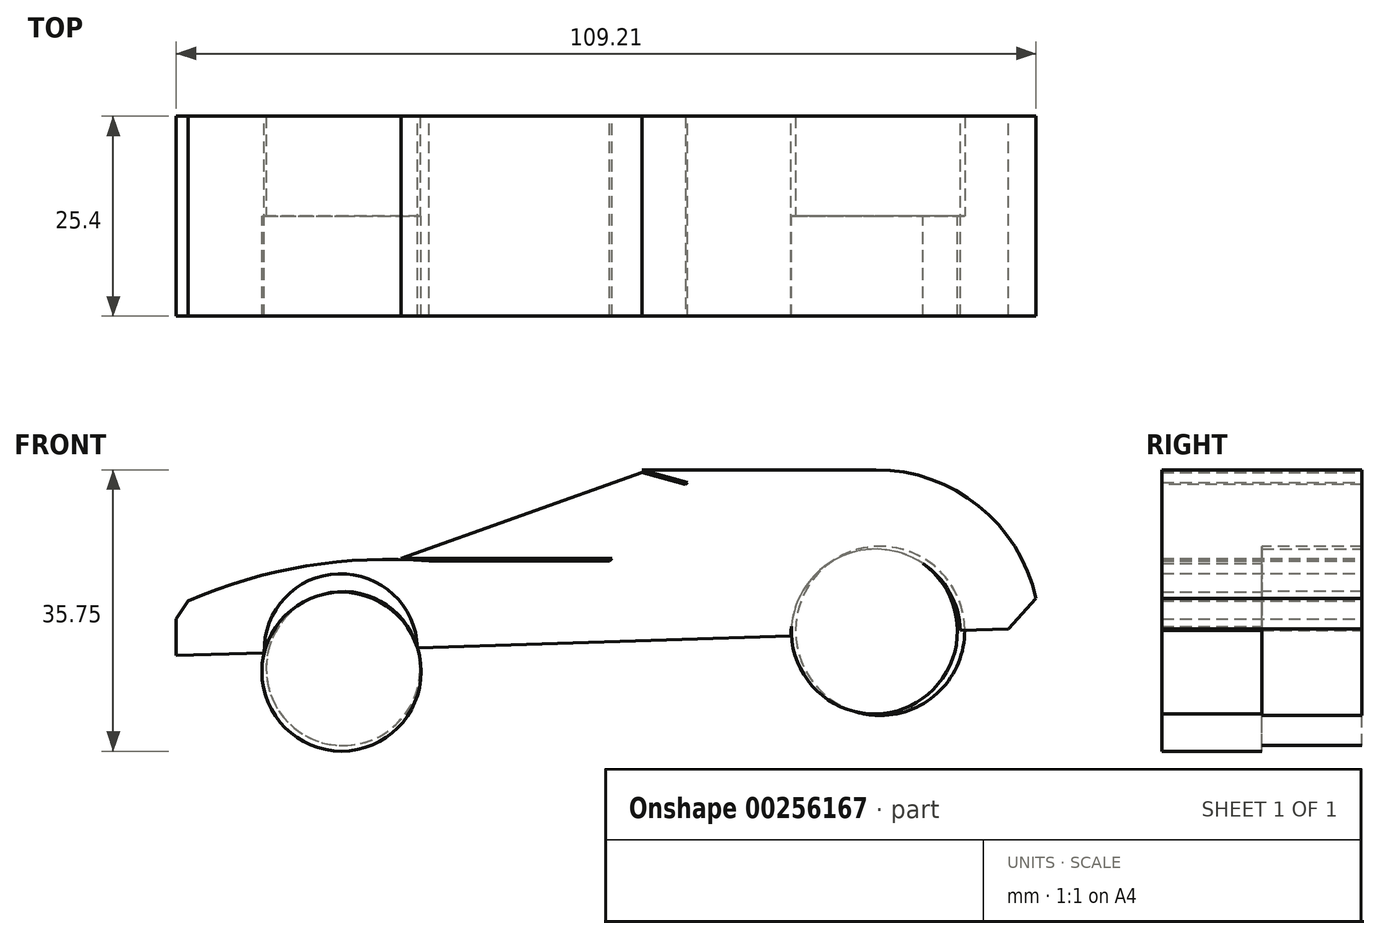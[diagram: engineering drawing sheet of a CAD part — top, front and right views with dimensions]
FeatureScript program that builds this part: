
annotation { "Feature Type Name" : "Feature", "Feature Type Description" : "" }
export const myFeature = defineFeature(function(context is Context, id is Id, definition is map)
    precondition{}
    {
        {
            var Q0;
            Q0=qCreatedBy(makeId("Front.planeOp"),FACE);
            var sketch = newSketch(context, id + "F0", { "sketchPlane" : qUnion([Q0])});
            skLineSegment(sketch, "E0.bottom", {"start": v(-59.18, 0) * mm, "end": v(59.18, 0) * mm});
            skLineSegment(sketch, "E0.top", {"start": v(-59.18, 31.34) * mm, "end": v(59.18, 31.34) * mm});
            skLineSegment(sketch, "E0.left", {"start": v(-59.18, 0) * mm, "end": v(-59.18, 31.34) * mm});
            skLineSegment(sketch, "E0.right", {"start": v(59.18, 0) * mm, "end": v(59.18, 31.34) * mm});
            skPoint(sketch, "E0.middle", {"position": v(0, 15.67) * mm});
            skArc(sketch, "E1", {"start": v(-27.1, 15.49) * mm, "mid": v(-43.51, 14.72) * mm, "end": v(-59.18, 9.77) * mm});
            skLineSegment(sketch, "E2", {"start": v(-27.1, 15.49) * mm, "end": v(0, 27.1) * mm});
            skLineSegment(sketch, "E3", {"start": v(0, 27.1) * mm, "end": v(29.68, 27.1) * mm});
            skArc(sketch, "E4", {"start": v(50.51, 7) * mm, "mid": v(44.15, 21.26) * mm, "end": v(29.68, 27.1) * mm});
            skLineSegment(sketch, "E5", {"start": v(-59.18, 3.5) * mm, "end": v(50.51, 7) * mm});
            skCircle(sketch, "E6", {"center": v(-38.28, 4.17) * mm, "radius": 9.73 * mm});
            skCircle(sketch, "E7", {"center": v(29.68, 6.25) * mm, "radius": 10.76 * mm});
            skLineSegment(sketch, "E8", {"start": v(46.52, 6.88) * mm, "end": v(50.03, 10.76) * mm});
            skLineSegment(sketch, "E9", {"start": v(-27.1, 15.49) * mm, "end": v(-4.17, 15.49) * mm});
            skLineSegment(sketch, "E10", {"start": v(-4.17, 15.49) * mm, "end": v(5.76, 25.5) * mm});
            skLineSegment(sketch, "E11", {"start": v(5.76, 25.5) * mm, "end": v(0, 27.1) * mm});
            skSolve(sketch);
        }
        {
            var Q0;
            {var subQ10=sQuery(id+"F0.wireOp",EDGE,"E1");Q0=makeQuery(id+"F0.imprint","IMPRINT",FACE,{"disambiguationData":[TD([[makeQuery(id+"F0.imprint","IMPRINT",EDGE,{"derivedFrom":subQ10}),1.0]])]});}
            extrude(context, id + "F1", {"entities" : qUnion([Q0]), "endBound" : BoundingType.SYMMETRIC, "depth" : 25.4 * mm});
        }
        {
            var Q0;
            Q0=qCreatedBy(makeId("Front.planeOp"),FACE);
            var sketch = newSketch(context, id + "F2", { "sketchPlane" : qUnion([Q0])});
            skLineSegment(sketch, "E12", {"start": v(-32, 14.65) * mm, "end": v(0, 26.92) * mm});
            skCircle(sketch, "E13", {"center": v(-38.2, 1.45) * mm, "radius": 10.1 * mm});
            skSolve(sketch);
        }
        {
            var Q0;
            Q0=makeQuery(id+"F2.imprint","IMPRINT",FACE,{"disambiguationData":[TD([[makeQuery(id+"F2.imprint","IMPRINT",EDGE,{"derivedFrom":sQuery(id+"F2.wireOp",EDGE,"E13")}),1.0]])]});
            extrude(context, id + "F3", {"entities" : qUnion([Q0]), "depth" : 12.7 * mm});
        }
        {
            var Q0;
            Q0=qCreatedBy(makeId("Front.planeOp"),FACE);
            var sketch = newSketch(context, id + "F4", { "sketchPlane" : qUnion([Q0])});
            skCircle(sketch, "E14", {"center": v(29.5, 6.64) * mm, "radius": 10.55 * mm});
            skSolve(sketch);
        }
        {
            var Q0;
            Q0 = qSketchRegion(id + "F4", true);
            extrude(context, id + "F5", {"entities" : qUnion([Q0]), "operationType" : NewBodyOperationType.ADD, "depth" : 12.7 * mm});
        }
        {
            var Q0;
            Q0=qCreatedBy(makeId("Front.planeOp"),FACE);
            var sketch = newSketch(context, id + "F6", { "sketchPlane" : qUnion([Q0])});
            skCircle(sketch, "E15", {"center": v(30.23, 6.64) * mm, "radius": 10.74 * mm});
            skCircle(sketch, "E16", {"center": v(-37.98, 1.84) * mm, "radius": 9.78 * mm});
            skSolve(sketch);
        }
        {
            var Q0;
            Q0=makeQuery(id+"F6.imprint","IMPRINT",FACE,{"disambiguationData":[TD([[makeQuery(id+"F6.imprint","IMPRINT",EDGE,{"derivedFrom":sQuery(id+"F6.wireOp",EDGE,"E15")}),1.0]])]});
            var Q1;
            Q1=makeQuery(id+"F6.imprint","IMPRINT",FACE,{"disambiguationData":[TD([[makeQuery(id+"F6.imprint","IMPRINT",EDGE,{"derivedFrom":sQuery(id+"F6.wireOp",EDGE,"E16")}),1.0]])]});
            extrude(context, id + "F7", {"entities" : qUnion([Q0, Q1]), "oppositeDirection" : true, "depth" : 12.7 * mm});
        }
        {
            var Q0;
            Q0=qCreatedBy(makeId("Front.planeOp"),FACE);
            var sketch = newSketch(context, id + "F8", { "sketchPlane" : qUnion([Q0])});
            skLineSegment(sketch, "E17", {"start": v(-30.6, 15.85) * mm, "end": v(-3.69, 15.85) * mm});
            skLineSegment(sketch, "E18", {"start": v(-3.69, 15.85) * mm, "end": v(5.53, 25.26) * mm});
            skLineSegment(sketch, "E19", {"start": v(5.53, 25.26) * mm, "end": v(0, 26.73) * mm});
            skLineSegment(sketch, "E20", {"start": v(-30.6, 15.85) * mm, "end": v(0, 26.73) * mm});
            skSolve(sketch);
        }
        {
            var Q0;
            Q0 = qSketchRegion(id + "F8", true);
            extrude(context, id + "F9", {"entities" : qUnion([Q0]), "operationType" : NewBodyOperationType.ADD, "endBound" : BoundingType.SYMMETRIC, "depth" : 25.4 * mm});
        }
        {
            var Q0;
            Q0=makeQuery(id+"F1.opExtrude","SWEPT_EDGE",EDGE,{"disambiguationData":[OSD([sQuery(id+"F0.wireOp",EDGE,"E0.left"),sQuery(id+"F0.wireOp",EDGE,"E1")])]});
            chamfer(context, id + "F10", {"entities" : qUnion([Q0]), "width" : 2.54 * mm, "tangentPropagation" : true});
        }
    });
